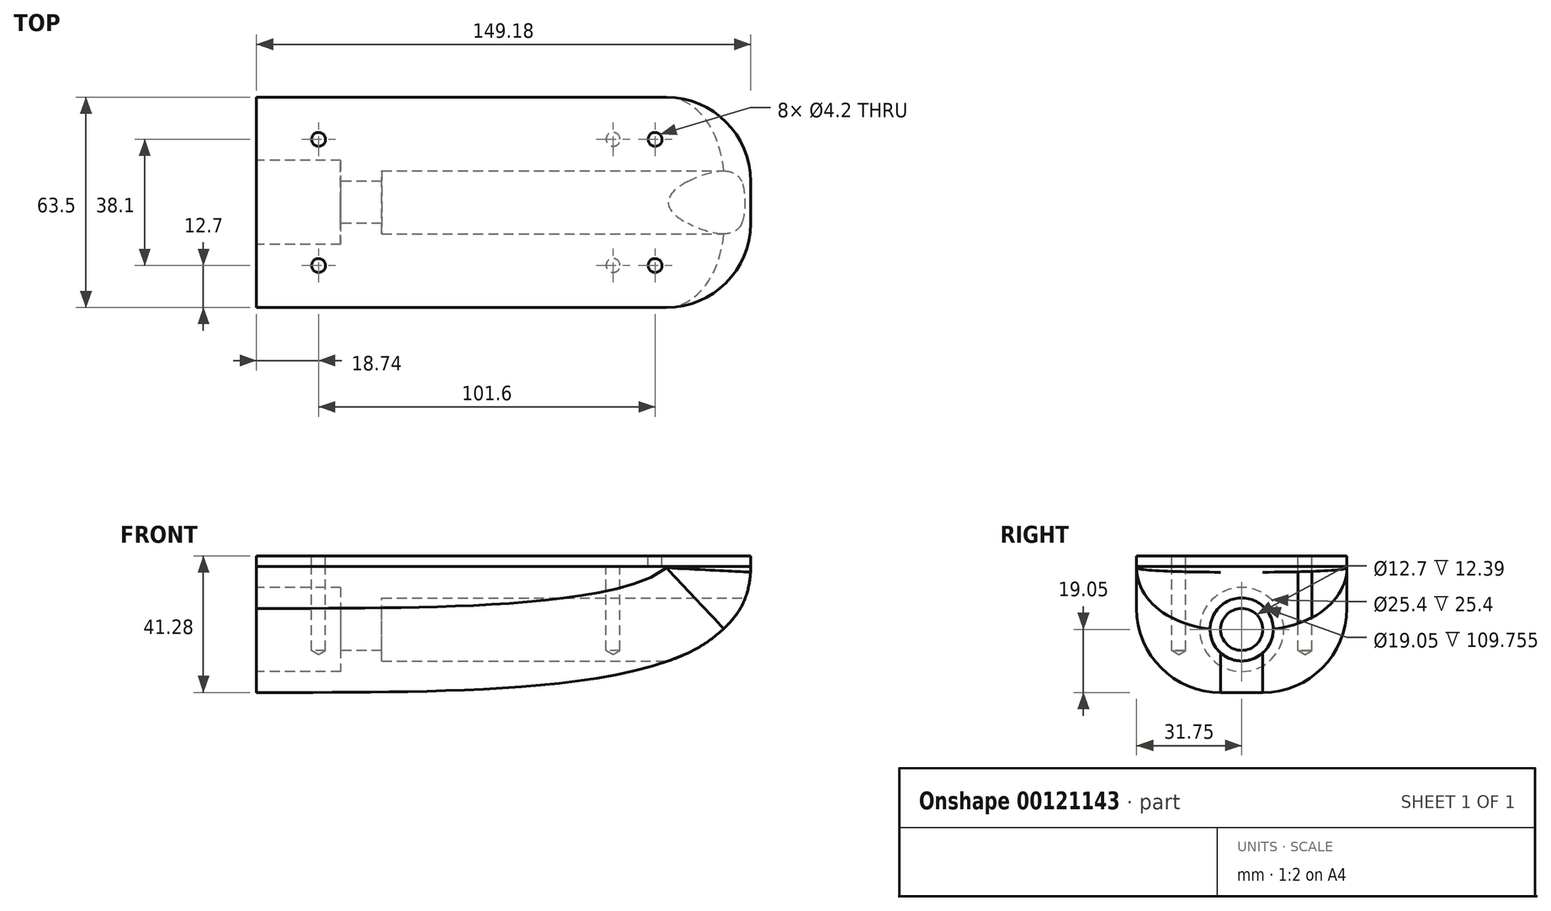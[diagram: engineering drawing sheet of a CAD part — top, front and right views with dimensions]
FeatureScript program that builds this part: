
annotation { "Feature Type Name" : "Feature", "Feature Type Description" : "" }
export const myFeature = defineFeature(function(context is Context, id is Id, definition is map)
    precondition{}
    {
        {
            var Q0;
            Q0=qCreatedBy(makeId("Front.planeOp"),FACE);
            var sketch = newSketch(context, id + "F0", { "sketchPlane" : qUnion([Q0])});
            skPoint(sketch, "E0.middle", {"position": v(0, 0) * mm});
            skLineSegment(sketch, "E1", {"start": v(-82.24, 19.05) * mm, "end": v(66.94, 19.05) * mm});
            skLineSegment(sketch, "E2", {"start": v(-82.24, 19.05) * mm, "end": v(-82.24, -19.05) * mm});
            skFitSpline(sketch, "E3", {"points": [v(-82.24, -19.05) * mm, v(66.94, 19.05) * mm], "startDerivative": vector(246.72, 0) * mm, "endDerivative": vector(0, 114.3) * mm});
            skSolve(sketch);
        }
        {
            var Q0;
            Q0=qSketchRegion(id+"F0",true);
            extrude(context, id + "F1", {"entities" : qUnion([Q0]), "depth" : 31.75 * mm, "hasSecondDirection" : true, "secondDirectionOppositeDirection" : true, "secondDirectionDepth" : 31.75 * mm});
        }
        {
            var Q0;
            Q0=makeQuery(id+"F1.opExtrude","CAP_EDGE",EDGE,{"disambiguationData":[OSD([sQuery(id+"F0.wireOp",EDGE,"E3")])],"isStart":false});
            var Q1;
            Q1=makeQuery(id+"F1.opExtrude","CAP_EDGE",EDGE,{"disambiguationData":[OSD([sQuery(id+"F0.wireOp",EDGE,"E3")])],"isStart":true});
            fillet(context, id + "F2", {"entities" : qUnion([Q0, Q1]), "radius" : 25.4 * mm, "tangentPropagation" : true, "allowEdgeOverflow" : false});
        }
        {
            var Q0;
            Q0=makeQuery(id+"F1.opExtrude","SWEPT_FACE",FACE,{"disambiguationData":[OSD([sQuery(id+"F0.wireOp",EDGE,"E2")])]});
            var sketch = newSketch(context, id + "F3", { "sketchPlane" : qUnion([Q0])});
            skCircle(sketch, "E4", {"center": v(0, 0) * mm, "radius": 6.35 * mm});
            skSolve(sketch);
        }
        {
            var Q0;
            Q0=qSketchRegion(id+"F3",true);
            extrude(context, id + "F4", {"entities" : qUnion([Q0]), "operationType" : NewBodyOperationType.REMOVE, "endBound" : BoundingType.THROUGH_ALL, "oppositeDirection" : true, "depth" : 25.4 * mm});
        }
        {
            var Q0;
            Q0=makeQuery(id+"F1.opExtrude","SWEPT_FACE",FACE,{"disambiguationData":[OSD([sQuery(id+"F0.wireOp",EDGE,"E2")])]});
            var sketch = newSketch(context, id + "F5", { "sketchPlane" : qUnion([Q0])});
            skCircle(sketch, "E5", {"center": v(0, 0) * mm, "radius": 12.7 * mm});
            skSolve(sketch);
        }
        {
            var Q0;
            Q0=qSketchRegion(id+"F5",true);
            extrude(context, id + "F6", {"entities" : qUnion([Q0]), "operationType" : NewBodyOperationType.REMOVE, "oppositeDirection" : true, "depth" : 25.4 * mm});
        }
        {
            var Q0;
            Q0=qCreatedBy(makeId("Right.planeOp"),FACE);
            var sketch = newSketch(context, id + "F7", { "sketchPlane" : qUnion([Q0])});
            skCircle(sketch, "E6", {"center": v(0, 0) * mm, "radius": 9.53 * mm});
            skSolve(sketch);
        }
        {
            var Q0;
            Q0=qSketchRegion(id+"F7",true);
            extrude(context, id + "F8", {"entities" : qUnion([Q0]), "operationType" : NewBodyOperationType.REMOVE, "oppositeDirection" : true, "depth" : 44.45 * mm, "hasSecondDirection" : true, "secondDirectionBound" : SecondDirectionBoundingType.THROUGH_ALL, "secondDirectionOppositeDirection" : false, "secondDirectionDepth" : 25.4 * mm});
        }
        {
            var Q0;
            Q0=makeQuery(id+"F1.opExtrude","SWEPT_FACE",FACE,{"disambiguationData":[OSD([sQuery(id+"F0.wireOp",EDGE,"E1")])]});
            var sketch = newSketch(context, id + "F9", { "sketchPlane" : qUnion([Q0])});
            skPoint(sketch, "E7", {"position": v(-63.5, 19.05) * mm});
            skPoint(sketch, "E8", {"position": v(-63.5, -19.05) * mm});
            skPoint(sketch, "E9", {"position": v(25.4, -19.05) * mm});
            skPoint(sketch, "E10", {"position": v(25.4, 19.05) * mm});
            skSolve(sketch);
        }
        {
            var Q0;
            Q0=sQuery(id+"F9.wireOp",VERTEX,"E7");
            var Q1;
            Q1=sQuery(id+"F9.wireOp",VERTEX,"E8");
            var Q2;
            Q2=sQuery(id+"F9.wireOp",VERTEX,"E10");
            var Q3;
            Q3=sQuery(id+"F9.wireOp",VERTEX,"E9");
            var Q4;
            Q4=makeQuery(id+"F1.opExtrude","SWEPT_BODY",BODY,{"disambiguationData":[OSD([sQuery(id+"F0.wireOp",EDGE,"E1"),sQuery(id+"F0.wireOp",EDGE,"E2"),sQuery(id+"F0.wireOp",EDGE,"E3")])]});
            hole(context, id + "F10", {"style" : HoleStyle.SIMPLE, "endStyle" : HoleEndStyle.BLIND, "standardTappedOrClearance" : lookupTablePath({ "standard" : "ISO", "engagement" : "75%", "pitch" : "0.8 mm", "size" : "M5", "type" : "Tapped" }), "standardBlindInLast" : lookupTablePath({ "standard" : "ISO", "engagement" : "75%", "pitch" : "0.8 mm", "size" : "M5", "type" : "Tapped" }), "holeDiameter" : 4.2 * mm, "holeDepth" : 25.4 * mm, "startFromSketch" : true, "locations" : qUnion([Q0, Q1, Q2, Q3]), "scope" : qUnion([Q4]), "majorDiameter" : 5 * mm});
        }
        {
            var Q0;
            Q0=makeQuery(id+"F1.opExtrude","SWEPT_FACE",FACE,{"disambiguationData":[OSD([sQuery(id+"F0.wireOp",EDGE,"E1")])]});
            var sketch = newSketch(context, id + "F11", { "sketchPlane" : qUnion([Q0])});
            skLineSegment(sketch, "E11.bottom", {"start": v(-82.24, 31.75) * mm, "end": v(41.54, 31.75) * mm});
            skLineSegment(sketch, "E11.top", {"start": v(-82.24, -31.75) * mm, "end": v(41.54, -31.75) * mm});
            skLineSegment(sketch, "E11.left", {"start": v(-82.24, 31.75) * mm, "end": v(-82.24, -31.75) * mm});
            skLineSegment(sketch, "E12", {"start": v(66.94, 6.35) * mm, "end": v(66.94, -6.35) * mm});
            skArc(sketch, "E13.0", {"start": v(66.94, 6.35) * mm, "mid": v(59.5, 24.31) * mm, "end": v(41.54, 31.75) * mm});
            skArc(sketch, "E14.0", {"start": v(41.54, -31.75) * mm, "mid": v(59.5, -24.31) * mm, "end": v(66.94, -6.35) * mm});
            skSolve(sketch);
        }
        {
            var Q0;
            Q0 = qSketchRegion(id + "F11", true);
            extrude(context, id + "F12", {"entities" : qUnion([Q0]), "depth" : 3.17 * mm});
        }
        {
            var Q0;
            Q0=makeQuery(id+"F12.opExtrude","CAP_FACE",FACE,{"disambiguationData":[OSD([sQuery(id+"F11.wireOp",EDGE,"E11.bottom"),sQuery(id+"F11.wireOp",EDGE,"E11.top"),sQuery(id+"F11.wireOp",EDGE,"E11.left"),sQuery(id+"F11.wireOp",EDGE,"E12"),sQuery(id+"F11.wireOp",EDGE,"E13.0"),sQuery(id+"F11.wireOp",EDGE,"E14.0")])],"isStart":false});
            var sketch = newSketch(context, id + "F13", { "sketchPlane" : qUnion([Q0])});
            skPoint(sketch, "E15", {"position": v(-63.5, 19.05) * mm});
            skPoint(sketch, "E16", {"position": v(-63.5, -19.05) * mm});
            skPoint(sketch, "E17", {"position": v(38.1, -19.05) * mm});
            skPoint(sketch, "E18", {"position": v(38.1, 19.05) * mm});
            skSolve(sketch);
        }
        {
            var Q0;
            Q0=sQuery(id+"F13.wireOp",VERTEX,"E15");
            var Q1;
            Q1=sQuery(id+"F13.wireOp",VERTEX,"E16");
            var Q2;
            Q2=sQuery(id+"F13.wireOp",VERTEX,"E17");
            var Q3;
            Q3=sQuery(id+"F13.wireOp",VERTEX,"E18");
            var Q4;
            Q4=makeQuery(id+"F12.opExtrude","SWEPT_BODY",BODY,{"disambiguationData":[OSD([sQuery(id+"F11.wireOp",EDGE,"E11.bottom"),sQuery(id+"F11.wireOp",EDGE,"E11.top"),sQuery(id+"F11.wireOp",EDGE,"E11.left"),sQuery(id+"F11.wireOp",EDGE,"E12"),sQuery(id+"F11.wireOp",EDGE,"E13.0"),sQuery(id+"F11.wireOp",EDGE,"E14.0")])]});
            hole(context, id + "F14", {"style" : HoleStyle.SIMPLE, "endStyle" : HoleEndStyle.THROUGH, "standardTappedOrClearance" : lookupTablePath({ "standard" : "ISO", "engagement" : "75%", "pitch" : "0.8 mm", "size" : "M5", "type" : "Tapped" }), "standardBlindInLast" : lookupTablePath({ "standard" : "ISO", "engagement" : "75%", "pitch" : "0.8 mm", "size" : "M5", "type" : "Tapped" }), "holeDiameter" : 4.2 * mm, "startFromSketch" : true, "locations" : qUnion([Q0, Q1, Q2, Q3]), "scope" : qUnion([Q4]), "isTappedThrough" : true, "majorDiameter" : 5 * mm, "showTappedDepth" : true});
        }
    });
